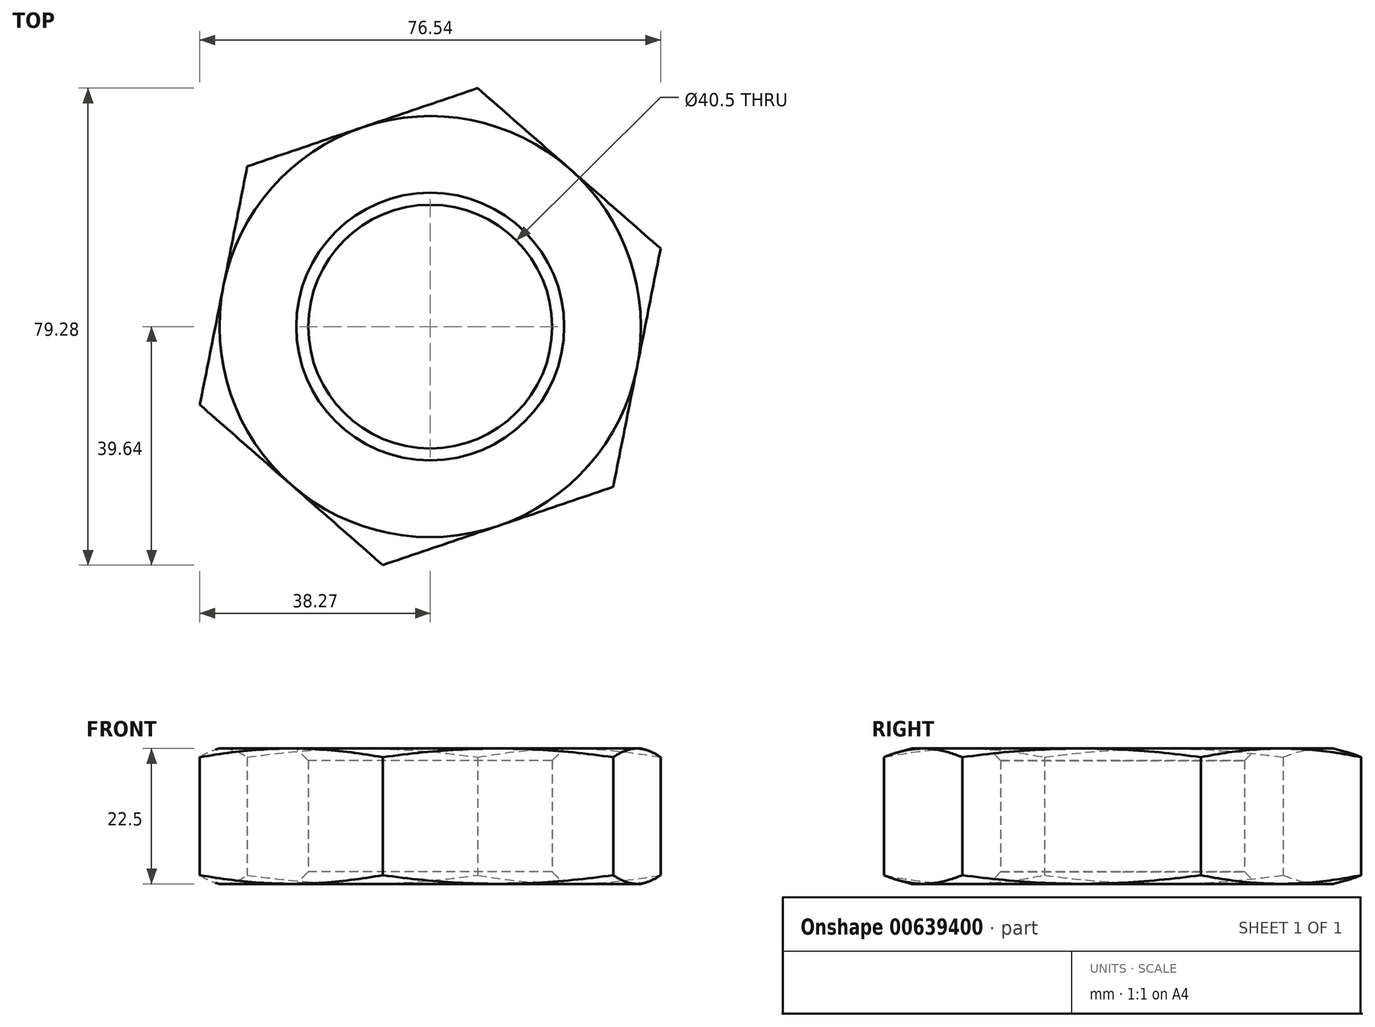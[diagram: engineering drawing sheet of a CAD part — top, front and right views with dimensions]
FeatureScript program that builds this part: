
annotation { "Feature Type Name" : "Feature", "Feature Type Description" : "" }
export const myFeature = defineFeature(function(context is Context, id is Id, definition is map)
    precondition{}
    {
        {
            var Q0;
            Q0=qCreatedBy(makeId("Top.planeOp"),FACE);
            var sketch = newSketch(context, id + "F0", { "sketchPlane" : qUnion([Q0])});
            skCircle(sketch, "E0.cCircle", {"center": v(0, 0) * mm, "radius": 35 * mm, "construction": true});
            skLineSegment(sketch, "E0.0", {"start": v(38.27, 13) * mm, "end": v(30.39, -26.65) * mm});
            skLineSegment(sketch, "E0.1", {"start": v(30.39, -26.65) * mm, "end": v(-7.88, -39.64) * mm});
            skLineSegment(sketch, "E0.2", {"start": v(-7.88, -39.64) * mm, "end": v(-38.27, -13) * mm});
            skLineSegment(sketch, "E0.3", {"start": v(-38.27, -13) * mm, "end": v(-30.39, 26.65) * mm});
            skLineSegment(sketch, "E0.4", {"start": v(-30.39, 26.65) * mm, "end": v(7.88, 39.64) * mm});
            skLineSegment(sketch, "E0.5", {"start": v(7.88, 39.64) * mm, "end": v(38.27, 13) * mm});
            skPoint(sketch, "E0.0.midPoint", {"position": v(34.33, -6.83) * mm});
            skCircle(sketch, "E1", {"center": v(0, 0) * mm, "radius": 20.25 * mm});
            skSolve(sketch);
        }
        {
            var Q0;
            Q0=makeQuery(id+"F0.imprint","IMPRINT",FACE,{"disambiguationData":[TD([[makeQuery(id+"F0.imprint","IMPRINT",EDGE,{"derivedFrom":sQuery(id+"F0.wireOp",EDGE,"E0.0")}),-1.0]])]});
            extrude(context, id + "F1", {"entities" : qUnion([Q0]), "depth" : 22.5 * mm, "offsetDistance" : 25 * mm});
        }
        {
            var Q0;
            Q0=makeQuery(id+"F1.opExtrude","CAP_FACE",FACE,{"disambiguationData":[OSD([sQuery(id+"F0.wireOp",EDGE,"E0.0"),sQuery(id+"F0.wireOp",EDGE,"E0.1"),sQuery(id+"F0.wireOp",EDGE,"E0.2"),sQuery(id+"F0.wireOp",EDGE,"E0.3"),sQuery(id+"F0.wireOp",EDGE,"E0.4"),sQuery(id+"F0.wireOp",EDGE,"E0.5"),sQuery(id+"F0.wireOp",EDGE,"E1")])],"isStart":false});
            var sketch = newSketch(context, id + "F2", { "sketchPlane" : qUnion([Q0])});
            skCircle(sketch, "E2", {"center": v(0, 0) * mm, "radius": 35 * mm});
            skSolve(sketch);
        }
        {
            var Q0;
            Q0=makeQuery(id+"F1.opExtrude","CAP_VERTEX",VERTEX,{"disambiguationData":[OSD([sQuery(id+"F0.wireOp",EDGE,"E0.0"),sQuery(id+"F0.wireOp",EDGE,"E0.5")])],"isStart":false});
            var Q1;
            Q1=makeQuery(id+"F1.opExtrude","CAP_VERTEX",VERTEX,{"disambiguationData":[OSD([sQuery(id+"F0.wireOp",EDGE,"E0.0"),sQuery(id+"F0.wireOp",EDGE,"E0.5")])],"isStart":true});
            var Q2;
            Q2=makeQuery(id+"F1.opExtrude","CAP_VERTEX",VERTEX,{"disambiguationData":[OSD([sQuery(id+"F0.wireOp",EDGE,"E0.2"),sQuery(id+"F0.wireOp",EDGE,"E0.3")])],"isStart":false});
            cPlane(context, id + "F3", {"entities" : qUnion([Q0, Q1, Q2]), "cplaneType" : CPlaneType.THREE_POINT, "offset" : 25 * mm, "width" : 150 * mm, "height" : 150 * mm});
        }
        {
            var Q0;
            Q0=qCreatedBy(id+"F3.planeOp",FACE);
            var sketch = newSketch(context, id + "F4", { "sketchPlane" : qUnion([Q0])});
            skLineSegment(sketch, "E3.0", {"start": v(-35, 22.5) * mm, "end": v(35, 22.5) * mm});
            skLineSegment(sketch, "E4", {"start": v(35, 22.5) * mm, "end": v(44.66, 19.91) * mm});
            skLineSegment(sketch, "E5", {"start": v(44.66, 19.91) * mm, "end": v(44.66, 22.7) * mm});
            skLineSegment(sketch, "E6", {"start": v(44.66, 22.7) * mm, "end": v(35, 22.7) * mm});
            skLineSegment(sketch, "E7", {"start": v(35, 22.7) * mm, "end": v(35, 22.5) * mm});
            skPoint(sketch, "E8.0", {"position": v(40.41, 11.25) * mm});
            skLineSegment(sketch, "E9", {"start": v(40.41, 11.25) * mm, "end": v(26.34, 11.25) * mm, "construction": true});
            skLineSegment(sketch, "E10.MirrorCS", {"start": v(35, 0) * mm, "end": v(44.66, 2.59) * mm});
            skLineSegment(sketch, "E11.MirrorCS", {"start": v(44.66, 2.59) * mm, "end": v(44.66, -0.2) * mm});
            skLineSegment(sketch, "E12.MirrorCS", {"start": v(44.66, -0.2) * mm, "end": v(35, -0.2) * mm});
            skLineSegment(sketch, "E13.MirrorCS", {"start": v(35, -0.2) * mm, "end": v(35, 0) * mm});
            skSolve(sketch);
        }
        {
            var Q0;
            Q0 = qSketchRegion(id + "F4", true);
            var Q1;
            Q1=makeQuery(id+"F1.opExtrude","SWEPT_FACE",FACE,{"disambiguationData":[OSD([sQuery(id+"F0.wireOp",EDGE,"E1")])]});
            revolve(context, id + "F5", {"operationType" : NewBodyOperationType.REMOVE, "entities" : qUnion([Q0]), "axis" : qUnion([Q1]), "revolveType" : RevolveType.FULL, "oppositeDirection" : true});
        }
        {
            var Q0;
            Q0=makeQuery(id+"F1.opExtrude","CAP_EDGE",EDGE,{"disambiguationData":[OSD([sQuery(id+"F0.wireOp",EDGE,"E1")])],"isStart":false});
            var Q1;
            Q1=makeQuery(id+"F1.opExtrude","CAP_EDGE",EDGE,{"disambiguationData":[OSD([sQuery(id+"F0.wireOp",EDGE,"E1")])],"isStart":true});
            chamfer(context, id + "F6", {"entities" : qUnion([Q0, Q1]), "width" : 2 * mm, "tangentPropagation" : true});
        }
    });
